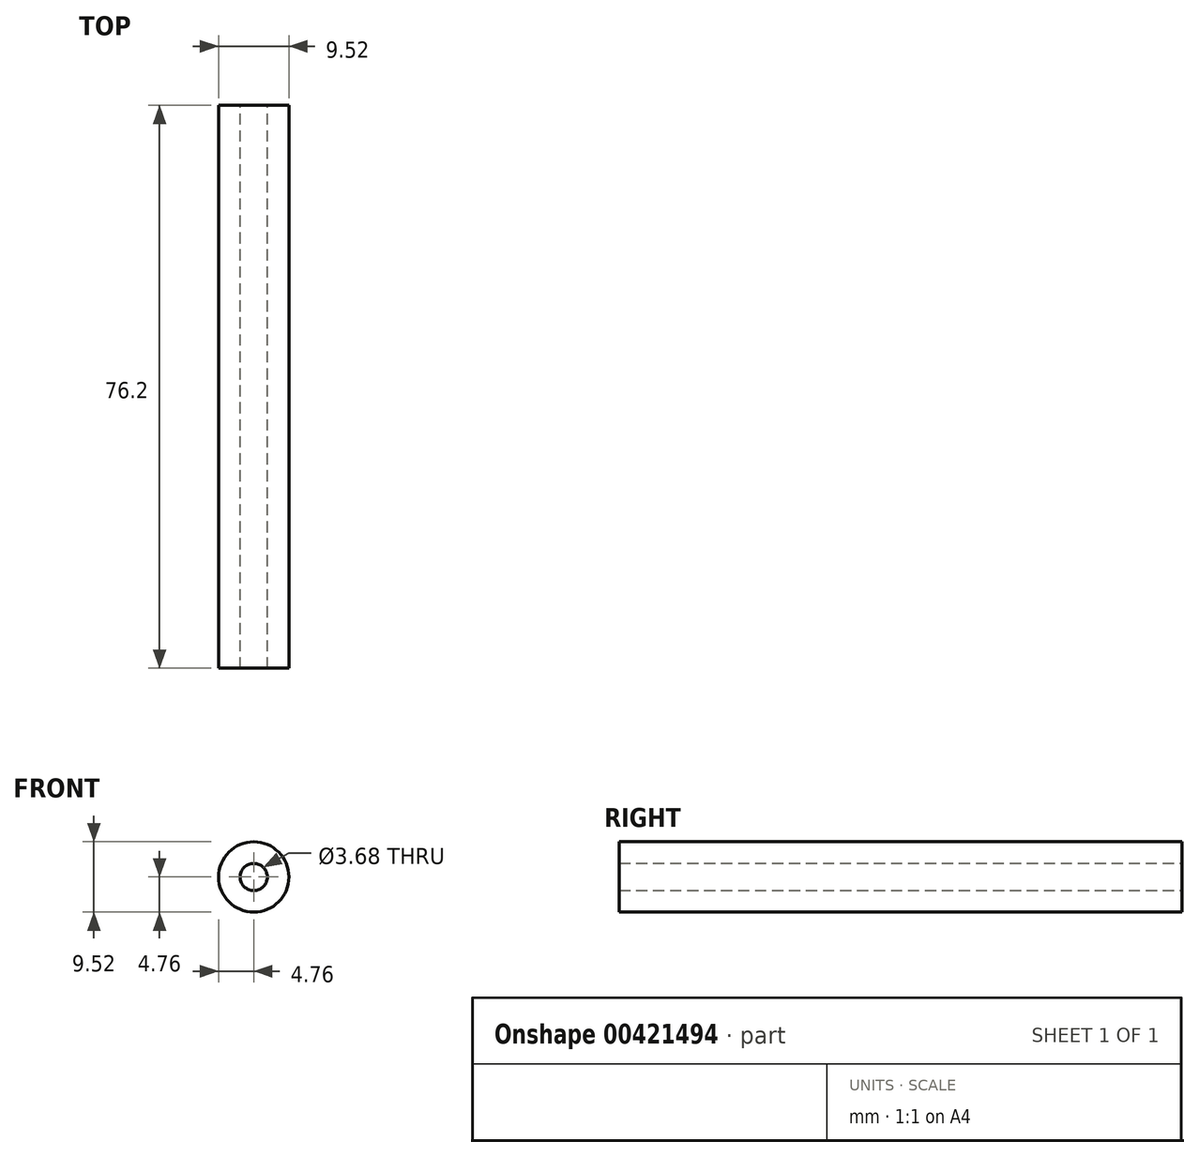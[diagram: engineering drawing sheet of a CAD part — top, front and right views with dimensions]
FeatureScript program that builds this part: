
annotation { "Feature Type Name" : "Feature", "Feature Type Description" : "" }
export const myFeature = defineFeature(function(context is Context, id is Id, definition is map)
    precondition{}
    {
        {
            var Q0;
            Q0=qCreatedBy(makeId("Front.planeOp"),FACE);
            var sketch = newSketch(context, id + "F0", { "sketchPlane" : qUnion([Q0])});
            skCircle(sketch, "E0", {"center": v(0, 0) * mm, "radius": 4.76 * mm});
            skCircle(sketch, "E1", {"center": v(0, 0) * mm, "radius": 1.84 * mm});
            skSolve(sketch);
        }
        {
            var Q0;
            Q0=qSketchRegion(id+"F0",true);
            var Q1;
            Q1=sQuery(id+"F0.wireOp",EDGE,"E0");
            extrude(context, id + "F1", {"entities" : qUnion([Q0]), "surfaceEntities" : qUnion([Q1]), "depth" : 76.2 * mm});
        }
    });
